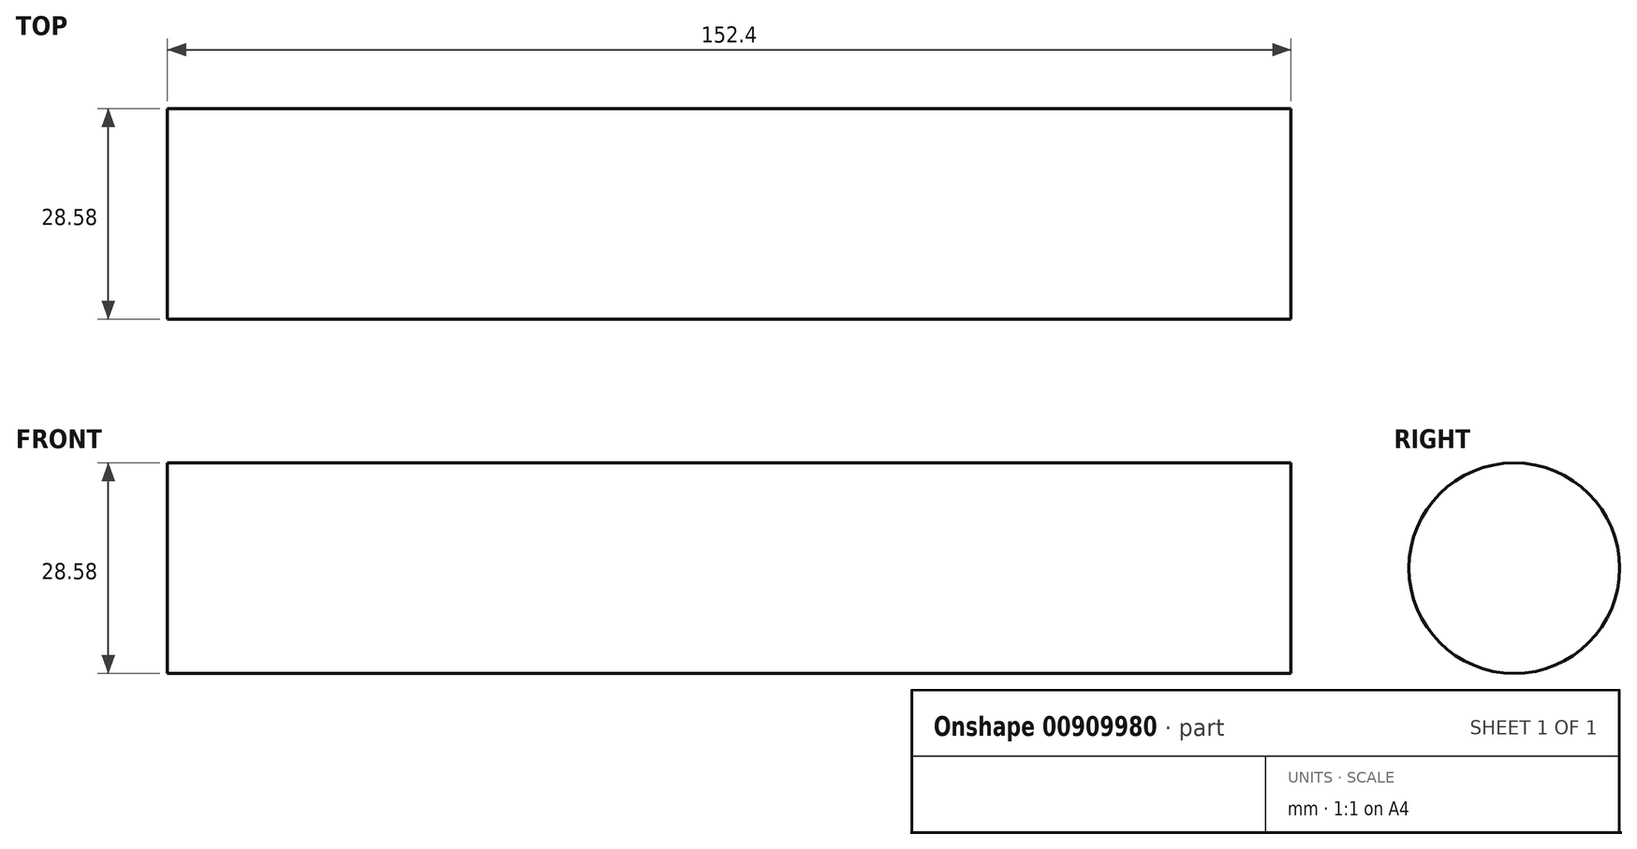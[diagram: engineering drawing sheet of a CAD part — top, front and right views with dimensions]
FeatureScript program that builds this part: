
annotation { "Feature Type Name" : "Feature", "Feature Type Description" : "" }
export const myFeature = defineFeature(function(context is Context, id is Id, definition is map)
    precondition{}
    {
        {
            var Q0;
            Q0=qCreatedBy(makeId("Right.planeOp"),FACE);
            var sketch = newSketch(context, id + "F0", { "sketchPlane" : qUnion([Q0])});
            skCircle(sketch, "E0", {"center": v(0, 0) * mm, "radius": 14.29 * mm});
            skSolve(sketch);
        }
        {
            var Q0;
            Q0=makeQuery(id+"F0.imprint","IMPRINT",FACE,{"disambiguationData":[TD([[makeQuery(id+"F0.imprint","IMPRINT",EDGE,{"derivedFrom":sQuery(id+"F0.wireOp",EDGE,"E0")}),1.0]])]});
            extrude(context, id + "F1", {"entities" : qUnion([Q0]), "oppositeDirection" : true, "depth" : 152.4 * mm, "offsetDistance" : 25 * mm});
        }
    });
